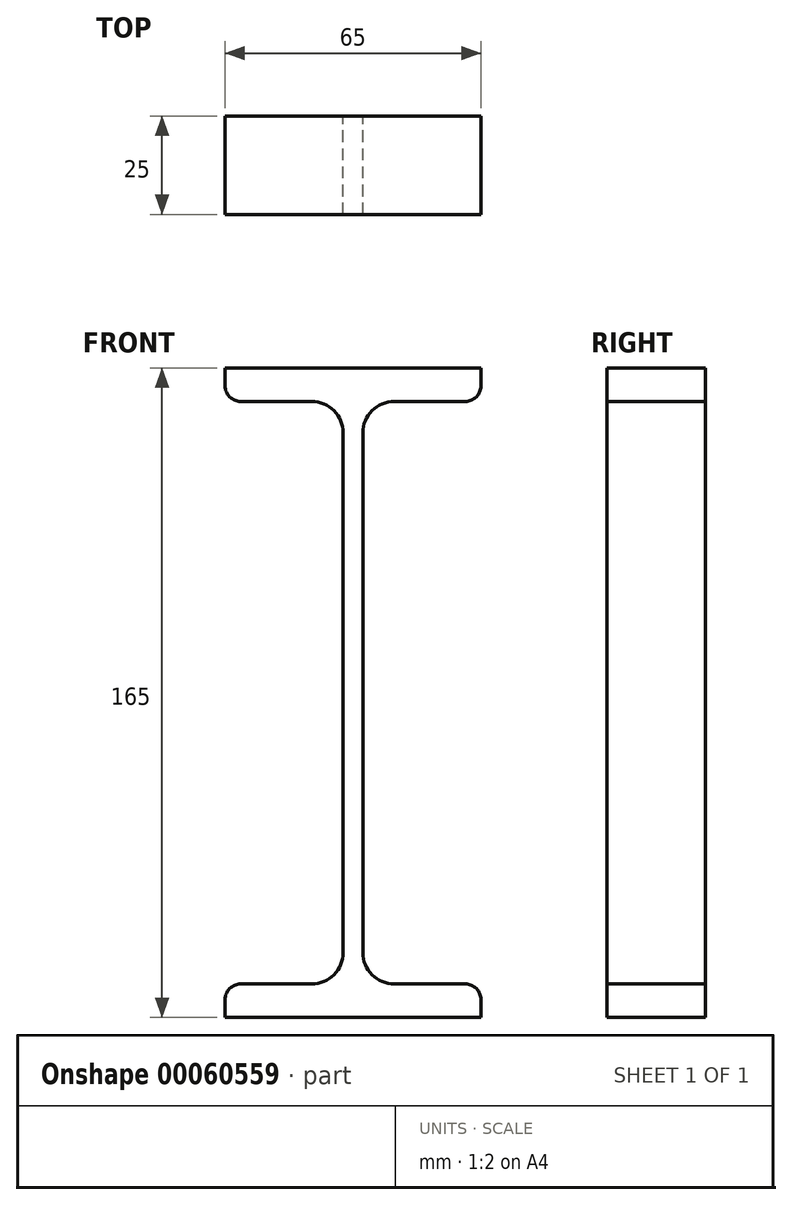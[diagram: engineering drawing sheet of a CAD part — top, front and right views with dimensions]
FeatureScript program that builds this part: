
annotation { "Feature Type Name" : "Feature", "Feature Type Description" : "" }
export const myFeature = defineFeature(function(context is Context, id is Id, definition is map)
    precondition{}
    {
        {
            var Q0;
            Q0=qCreatedBy(makeId("Front.planeOp"),FACE);
            var sketch = newSketch(context, id + "F0", { "sketchPlane" : qUnion([Q0])});
            skLineSegment(sketch, "E0", {"start": v(-32.5, 82.5) * mm, "end": v(32.5, 82.5) * mm});
            skLineSegment(sketch, "E1", {"start": v(32.5, 82.5) * mm, "end": v(32.5, 78) * mm});
            skLineSegment(sketch, "E2", {"start": v(28.5, 74) * mm, "end": v(10.5, 74) * mm});
            skLineSegment(sketch, "E3", {"start": v(-2.5, 66) * mm, "end": v(-2.5, -66) * mm});
            skLineSegment(sketch, "E4", {"start": v(10.5, -74) * mm, "end": v(28.5, -74) * mm});
            skLineSegment(sketch, "E5", {"start": v(32.5, -78) * mm, "end": v(32.5, -82.5) * mm});
            skLineSegment(sketch, "E6", {"start": v(32.5, -82.5) * mm, "end": v(-32.5, -82.5) * mm});
            skLineSegment(sketch, "E7", {"start": v(-32.5, -82.5) * mm, "end": v(-32.5, -78) * mm});
            skLineSegment(sketch, "E8", {"start": v(-28.5, -74) * mm, "end": v(-10.5, -74) * mm});
            skLineSegment(sketch, "E9", {"start": v(2.5, -66) * mm, "end": v(2.5, 66) * mm});
            skLineSegment(sketch, "E10", {"start": v(-10.5, 74) * mm, "end": v(-28.5, 74) * mm});
            skLineSegment(sketch, "E11", {"start": v(-32.5, 78) * mm, "end": v(-32.5, 82.5) * mm});
            skPoint(sketch, "E12.visualSharp", {"position": v(-2.5, 74) * mm});
            skArc(sketch, "E12.filletArc", {"start": v(-2.5, 66) * mm, "mid": v(-4.84, 71.66) * mm, "end": v(-10.5, 74) * mm});
            skPoint(sketch, "E13.visualSharp", {"position": v(2.5, 74) * mm});
            skArc(sketch, "E13.filletArc", {"start": v(10.5, 74) * mm, "mid": v(4.84, 71.66) * mm, "end": v(2.5, 66) * mm});
            skPoint(sketch, "E14.visualSharp", {"position": v(-2.5, -74) * mm});
            skArc(sketch, "E14.filletArc", {"start": v(-10.5, -74) * mm, "mid": v(-4.84, -71.66) * mm, "end": v(-2.5, -66) * mm});
            skPoint(sketch, "E15.visualSharp", {"position": v(2.5, -74) * mm});
            skArc(sketch, "E15.filletArc", {"start": v(2.5, -66) * mm, "mid": v(4.84, -71.66) * mm, "end": v(10.5, -74) * mm});
            skPoint(sketch, "E16.visualSharp", {"position": v(-32.5, 74) * mm});
            skArc(sketch, "E16.filletArc", {"start": v(-32.5, 78) * mm, "mid": v(-31.33, 75.17) * mm, "end": v(-28.5, 74) * mm});
            skPoint(sketch, "E17.visualSharp", {"position": v(32.5, 74) * mm});
            skArc(sketch, "E17.filletArc", {"start": v(28.5, 74) * mm, "mid": v(31.33, 75.17) * mm, "end": v(32.5, 78) * mm});
            skPoint(sketch, "E18.visualSharp", {"position": v(32.5, -74) * mm});
            skArc(sketch, "E18.filletArc", {"start": v(32.5, -78) * mm, "mid": v(31.33, -75.17) * mm, "end": v(28.5, -74) * mm});
            skPoint(sketch, "E19.visualSharp", {"position": v(-32.5, -74) * mm});
            skArc(sketch, "E19.filletArc", {"start": v(-28.5, -74) * mm, "mid": v(-31.33, -75.17) * mm, "end": v(-32.5, -78) * mm});
            skSolve(sketch);
        }
        {
            var Q0;
            Q0 = qSketchRegion(id + "F0", true);
            extrude(context, id + "F1", {"entities" : qUnion([Q0]), "depth" : 25 * mm});
        }
    });
